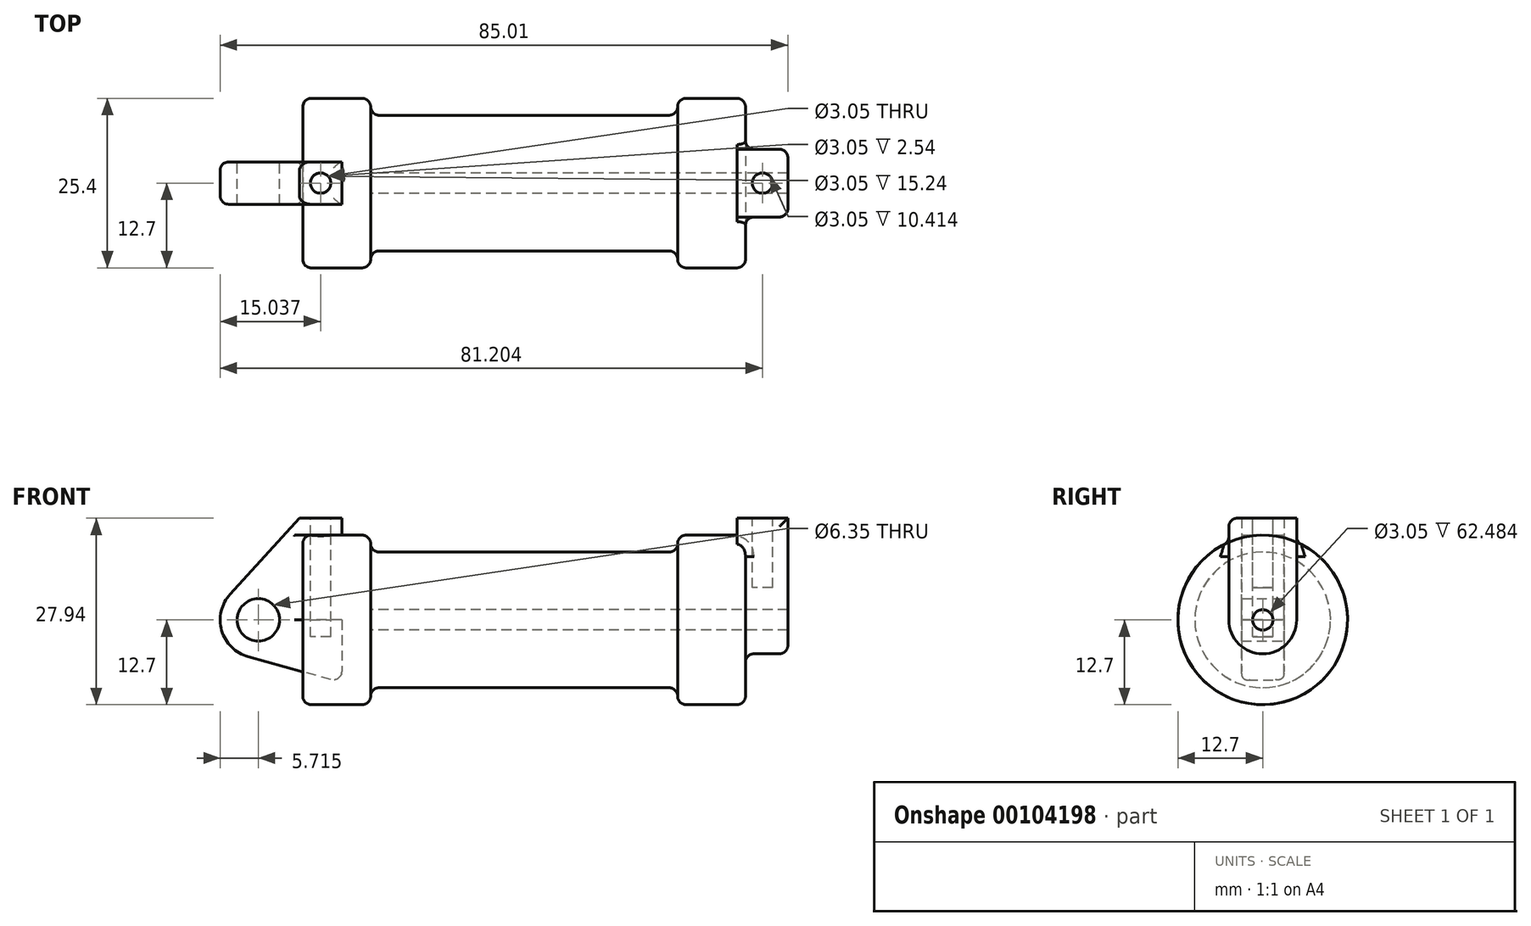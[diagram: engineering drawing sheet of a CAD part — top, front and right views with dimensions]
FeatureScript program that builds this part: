
annotation { "Feature Type Name" : "Feature", "Feature Type Description" : "" }
export const myFeature = defineFeature(function(context is Context, id is Id, definition is map)
    precondition{}
    {
        {
            var Q0;
            Q0=qCreatedBy(makeId("Front.planeOp"),FACE);
            var sketch = newSketch(context, id + "F0", { "sketchPlane" : qUnion([Q0])});
            skLineSegment(sketch, "E0", {"start": v(0, 0) * mm, "end": v(0, 12.7) * mm});
            skLineSegment(sketch, "E1", {"start": v(0, 12.7) * mm, "end": v(10.16, 12.7) * mm});
            skLineSegment(sketch, "E2", {"start": v(10.16, 12.7) * mm, "end": v(10.16, 10.16) * mm});
            skLineSegment(sketch, "E3", {"start": v(10.16, 10.16) * mm, "end": v(56.13, 10.16) * mm});
            skLineSegment(sketch, "E4", {"start": v(56.13, 10.16) * mm, "end": v(56.13, 12.7) * mm});
            skLineSegment(sketch, "E5", {"start": v(56.13, 12.7) * mm, "end": v(66.3, 12.7) * mm});
            skLineSegment(sketch, "E6", {"start": v(66.3, 12.7) * mm, "end": v(66.3, 0) * mm});
            skLineSegment(sketch, "E7", {"start": v(66.3, 0) * mm, "end": v(0, 0) * mm});
            skLineSegment(sketch, "E8", {"start": v(5.84, 15.24) * mm, "end": v(-0.5, 15.24) * mm});
            skLineSegment(sketch, "E9", {"start": v(-0.5, 15.24) * mm, "end": v(-10.88, 3.85) * mm});
            skLineSegment(sketch, "E10", {"start": v(0, 0) * mm, "end": v(-6.65, 0) * mm});
            skCircle(sketch, "E11", {"center": v(-6.65, 0) * mm, "radius": 5.72 * mm});
            skCircle(sketch, "E12", {"center": v(-6.65, 0) * mm, "radius": 3.18 * mm});
            skLineSegment(sketch, "E13", {"start": v(5.84, 15.24) * mm, "end": v(5.84, -9.4) * mm});
            skLineSegment(sketch, "E14", {"start": v(5.84, -9.4) * mm, "end": v(-8.18, -5.5) * mm});
            skSolve(sketch);
        }
        {
            var Q0;
            {var subQ0=sQuery(id+"F0.wireOp",EDGE,"E2");Q0=makeQuery(id+"F0.imprint","IMPRINT",FACE,{"disambiguationData":[TD([[makeQuery(id+"F0.imprint","IMPRINT",EDGE,{"derivedFrom":subQ0}),-1.0]])]});}
            var Q1;
            Q1=sQuery(id+"F0.wireOp",EDGE,"E7");
            revolve(context, id + "F1", {"entities" : qUnion([Q0]), "axis" : qUnion([Q1]), "revolveType" : RevolveType.FULL});
        }
        {
            var Q0;
            {var subQ0=sQuery(id+"F0.wireOp",EDGE,"E2");Q0=makeQuery(id+"F0.imprint","IMPRINT",FACE,{"disambiguationData":[TD([[makeQuery(id+"F0.imprint","IMPRINT",EDGE,{"derivedFrom":subQ0}),-1.0]])]});}
            var Q1;
            {var subQ0=sQuery(id+"F0.wireOp",EDGE,"E0");Q1=makeQuery(id+"F0.imprint","IMPRINT",FACE,{"disambiguationData":[TD([[makeQuery(id+"F0.imprint","IMPRINT",EDGE,{"derivedFrom":subQ0}),-1.0]])]});}
            var Q2;
            Q2=sQuery(id+"F0.wireOp",EDGE,"E7");
            revolve(context, id + "F2", {"entities" : qUnion([Q0, Q1]), "axis" : qUnion([Q2]), "revolveType" : RevolveType.FULL});
        }
        {
            var Q0;
            {var subQ3=sQuery(id+"F0.wireOp",EDGE,"E0");Q0=makeQuery(id+"F0.imprint","IMPRINT",FACE,{"disambiguationData":[TD([[makeQuery(id+"F0.imprint","IMPRINT",EDGE,{"derivedFrom":subQ3}),1.0]])]});}
            var Q1;
            {var subQ0=sQuery(id+"F0.wireOp",EDGE,"E14");Q1=makeQuery(id+"F0.imprint","IMPRINT",FACE,{"disambiguationData":[TD([[makeQuery(id+"F0.imprint","IMPRINT",EDGE,{"derivedFrom":subQ0}),-1.0]])]});}
            var Q2;
            {var subQ4=sQuery(id+"F0.wireOp",EDGE,"E12");Q2=makeQuery(id+"F0.imprint","IMPRINT",FACE,{"disambiguationData":[TD([[makeQuery(id+"F0.imprint","IMPRINT",EDGE,{"derivedFrom":subQ4}),-1.0]])]});}
            extrude(context, id + "F3", {"entities" : qUnion([Q0, Q1, Q2]), "endBound" : BoundingType.SYMMETRIC, "depth" : 6.35 * mm});
        }
        {
            var Q0;
            Q0=makeQuery(id+"F2.opRevolve","SWEPT_FACE",FACE,{"disambiguationData":[OSD([sQuery(id+"F0.wireOp",EDGE,"E6")])]});
            var sketch = newSketch(context, id + "F4", { "sketchPlane" : qUnion([Q0])});
            skCircle(sketch, "E15", {"center": v(0, 0) * mm, "radius": 5.08 * mm});
            skCircle(sketch, "E16", {"center": v(0, 0) * mm, "radius": 1.52 * mm});
            skLineSegment(sketch, "E17", {"start": v(0, 15.24) * mm, "end": v(-3.2, 15.24) * mm});
            skLineSegment(sketch, "E18", {"start": v(-3.2, 15.24) * mm, "end": v(-5.08, 15.24) * mm});
            skLineSegment(sketch, "E19", {"start": v(-5.08, 15.24) * mm, "end": v(-5.08, 0) * mm});
            skLineSegment(sketch, "E20", {"start": v(5.08, 0) * mm, "end": v(5.08, 15.24) * mm});
            skLineSegment(sketch, "E21", {"start": v(5.08, 15.24) * mm, "end": v(0, 15.24) * mm});
            skSolve(sketch);
        }
        {
            var Q0;
            {var subQ0=sQuery(id+"F4.wireOp",EDGE,"E19");var subQ1=sQuery(id+"F4.wireOp",EDGE,"E15");var subQ2=makeQuery(id+"F4.imprint","INTERSECT",VERTEX,{"derivedFrom":[subQ1,subQ0]});Q0=makeQuery(id+"F4.imprint","IMPRINT",FACE,{"disambiguationData":[TD([[makeQuery(id+"F4.imprint","IMPRINT",EDGE,{"disambiguationData":[TD([[subQ2,1.0]])],"derivedFrom":subQ1}),-1.0]])]});}
            var Q1;
            Q1=makeQuery(id+"F4.imprint","IMPRINT",FACE,{"disambiguationData":[TD([[makeQuery(id+"F4.imprint","IMPRINT",EDGE,{"derivedFrom":sQuery(id+"F4.wireOp",EDGE,"E16")}),-1.0]])]});
            var Q2;
            Q2=makeQuery(id+"F4.imprint","IMPRINT",FACE,{"disambiguationData":[TD([[makeQuery(id+"F4.imprint","IMPRINT",EDGE,{"derivedFrom":sQuery(id+"F4.wireOp",EDGE,"E17")}),1.0]])]});
            extrude(context, id + "F5", {"entities" : qUnion([Q0, Q1, Q2]), "operationType" : NewBodyOperationType.ADD, "depth" : 6.35 * mm});
        }
        {
            var Q0;
            Q0=makeQuery(id+"F5.opExtrude","CAP_FACE",FACE,{"disambiguationData":[OSD([sQuery(id+"F4.wireOp",EDGE,"E15"),sQuery(id+"F4.wireOp",EDGE,"E16"),sQuery(id+"F4.wireOp",EDGE,"E17"),sQuery(id+"F4.wireOp",EDGE,"E18"),sQuery(id+"F4.wireOp",EDGE,"E19"),sQuery(id+"F4.wireOp",EDGE,"E20"),sQuery(id+"F4.wireOp",EDGE,"E21")])],"isStart":true});
            extrude(context, id + "F6", {"entities" : qUnion([Q0]), "operationType" : NewBodyOperationType.ADD, "depth" : 1.27 * mm});
        }
        {
            var Q0;
            Q0=makeQuery(id+"F5.boolean.opBoolean","SPLIT",FACE,{"disambiguationData":[TD([makeQuery(id+"F5.opExtrude","SWEPT_FACE",FACE,{"disambiguationData":[OSD([sQuery(id+"F4.wireOp",EDGE,"E16")])]})])],"derivedFrom":makeQuery(id+"F1.opRevolve","SWEPT_FACE",FACE,{"disambiguationData":[OSD([sQuery(id+"F0.wireOp",EDGE,"E6")])]})});
            var Q1;
            Q1=makeQuery(id+"F1.opRevolve","SWEPT_FACE",FACE,{"disambiguationData":[OSD([sQuery(id+"F0.wireOp",EDGE,"E2")])]});
            extrude(context, id + "F7", {"entities" : qUnion([Q0]), "operationType" : NewBodyOperationType.REMOVE, "endBound" : BoundingType.UP_TO_SURFACE, "oppositeDirection" : true, "endBoundEntityFace" : qUnion([Q1]), "depth" : 25.4 * mm});
        }
        {
            var Q0;
            Q0=makeQuery(id+"F3.opExtrude","SWEPT_FACE",FACE,{"disambiguationData":[OSD([sQuery(id+"F0.wireOp",EDGE,"E8")])]});
            var sketch = newSketch(context, id + "F8", { "sketchPlane" : qUnion([Q0])});
            skCircle(sketch, "E22", {"center": v(2.67, 0) * mm, "radius": 1.52 * mm});
            skPoint(sketch, "E22.centerSnap0", {"position": v(-0.5, 0) * mm});
            skPoint(sketch, "E22.centerSnap1", {"position": v(2.67, -3.18) * mm});
            skSolve(sketch);
        }
        {
            var Q0;
            {var subQ0=sQuery(id+"F4.wireOp",EDGE,"E21");var subQ1=sQuery(id+"F4.wireOp",EDGE,"E18");var subQ2=sQuery(id+"F4.wireOp",EDGE,"E17");Q0=makeQuery(id+"F6.boolean.opBoolean","MERGE",FACE,{"derivedFrom":[makeQuery(id+"F5.opExtrude","SWEPT_FACE",FACE,{"disambiguationData":[OSD([subQ2,subQ1,subQ0])]}),makeQuery(id+"F6.opExtrude","SWEPT_FACE",FACE,{"disambiguationData":[OSD([subQ2,subQ1,subQ0])]})]});}
            var sketch = newSketch(context, id + "F9", { "sketchPlane" : qUnion([Q0])});
            skCircle(sketch, "E23", {"center": v(68.83, 0) * mm, "radius": 1.52 * mm});
            skPoint(sketch, "E23.centerSnap0", {"position": v(68.83, 5.08) * mm});
            skPoint(sketch, "E23.centerSnap1", {"position": v(65.02, 0) * mm});
            skSolve(sketch);
        }
        {
            var Q0;
            Q0=makeQuery(id+"F8.imprint","IMPRINT",FACE,{"disambiguationData":[TD([[makeQuery(id+"F8.imprint","IMPRINT",EDGE,{"derivedFrom":sQuery(id+"F8.wireOp",EDGE,"E22")}),1.0]])]});
            extrude(context, id + "F10", {"entities" : qUnion([Q0]), "operationType" : NewBodyOperationType.REMOVE, "oppositeDirection" : true, "depth" : 17.78 * mm});
        }
        {
            var Q0;
            Q0=makeQuery(id+"F9.imprint","IMPRINT",FACE,{"disambiguationData":[TD([[makeQuery(id+"F9.imprint","IMPRINT",EDGE,{"derivedFrom":sQuery(id+"F9.wireOp",EDGE,"E23")}),1.0]])]});
            extrude(context, id + "F11", {"entities" : qUnion([Q0]), "operationType" : NewBodyOperationType.REMOVE, "oppositeDirection" : true, "depth" : 10.4 * mm});
        }
        {
            var Q0;
            Q0=makeQuery(id+"F1.opRevolve","SWEPT_EDGE",EDGE,{"disambiguationData":[OSD([sQuery(id+"F0.wireOp",EDGE,"E3"),sQuery(id+"F0.wireOp",EDGE,"E4")])]});
            var Q1;
            Q1=makeQuery(id+"F1.opRevolve","SWEPT_EDGE",EDGE,{"disambiguationData":[OSD([sQuery(id+"F0.wireOp",EDGE,"E1"),sQuery(id+"F0.wireOp",EDGE,"E2")])]});
            var Q2;
            Q2=makeQuery(id+"F1.opRevolve","SWEPT_EDGE",EDGE,{"disambiguationData":[OSD([sQuery(id+"F0.wireOp",EDGE,"E2"),sQuery(id+"F0.wireOp",EDGE,"E3")])]});
            var Q3;
            Q3=makeQuery(id+"F1.opRevolve","SWEPT_EDGE",EDGE,{"disambiguationData":[OSD([sQuery(id+"F0.wireOp",EDGE,"E4"),sQuery(id+"F0.wireOp",EDGE,"E5")])]});
            fillet(context, id + "F12", {"entities" : qUnion([Q0, Q1, Q2, Q3]), "radius" : 1.27 * mm, "allowEdgeOverflow" : false});
        }
        {
            var Q0;
            {var subQ0=sQuery(id+"F0.wireOp",EDGE,"E6");Q0=makeQuery(id+"F5.boolean.opBoolean","INTERSECT",EDGE,{"disambiguationData":[OD(3.0)],"derivedFrom":[makeQuery(id+"F1.opRevolve","SWEPT_FACE",FACE,{"disambiguationData":[OSD([subQ0])]}),makeQuery(id+"F2.opRevolve","SWEPT_FACE",FACE,{"disambiguationData":[OSD([subQ0])]})]});}
            var Q1;
            Q1=makeQuery(id+"F5.boolean.opBoolean","SPLIT",EDGE,{"derivedFrom":makeQuery(id+"F1.opRevolve","SWEPT_EDGE",EDGE,{"disambiguationData":[OSD([sQuery(id+"F0.wireOp",EDGE,"E5"),sQuery(id+"F0.wireOp",EDGE,"E6")])]})});
            fillet(context, id + "F13", {"entities" : qUnion([Q0, Q1]), "radius" : 1.27 * mm, "tangentPropagation" : true, "allowEdgeOverflow" : false});
        }
        {
            var Q0;
            Q0=makeQuery(id+"F5.opExtrude","CAP_EDGE",EDGE,{"disambiguationData":[OSD([sQuery(id+"F4.wireOp",EDGE,"E19")])],"isStart":false});
            var Q1;
            {var subQ0=sQuery(id+"F4.wireOp",EDGE,"E19");var subQ1=sQuery(id+"F4.wireOp",EDGE,"E18");Q1=makeQuery(id+"F6.boolean.opBoolean","MERGE",EDGE,{"derivedFrom":[makeQuery(id+"F5.opExtrude","SWEPT_EDGE",EDGE,{"disambiguationData":[OSD([subQ1,subQ0])]}),makeQuery(id+"F6.opExtrude","SWEPT_EDGE",EDGE,{"disambiguationData":[OSD([subQ1,subQ0])]})]});}
            fillet(context, id + "F14", {"entities" : qUnion([Q0, Q1]), "radius" : 1.27 * mm, "tangentPropagation" : true, "allowEdgeOverflow" : false});
        }
        {
            var Q0;
            Q0=makeQuery(id+"F2.opRevolve","SWEPT_EDGE",EDGE,{"disambiguationData":[OSD([sQuery(id+"F0.wireOp",EDGE,"E0"),sQuery(id+"F0.wireOp",EDGE,"E1")])]});
            var Q1;
            Q1=makeQuery(id+"F3.opExtrude","SWEPT_FACE",FACE,{"disambiguationData":[OSD([sQuery(id+"F0.wireOp",EDGE,"E14")])]});
            var Q2;
            Q2=makeQuery(id+"F3.opExtrude","CAP_EDGE",EDGE,{"disambiguationData":[OSD([sQuery(id+"F0.wireOp",EDGE,"E0")])],"isStart":true});
            var Q3;
            Q3=makeQuery(id+"F3.opExtrude","CAP_EDGE",EDGE,{"disambiguationData":[OSD([sQuery(id+"F0.wireOp",EDGE,"E0")])],"isStart":false});
            fillet(context, id + "F15", {"entities" : qUnion([Q0, Q1, Q2, Q3]), "radius" : 1.27 * mm, "tangentPropagation" : true, "allowEdgeOverflow" : false});
        }
    });
